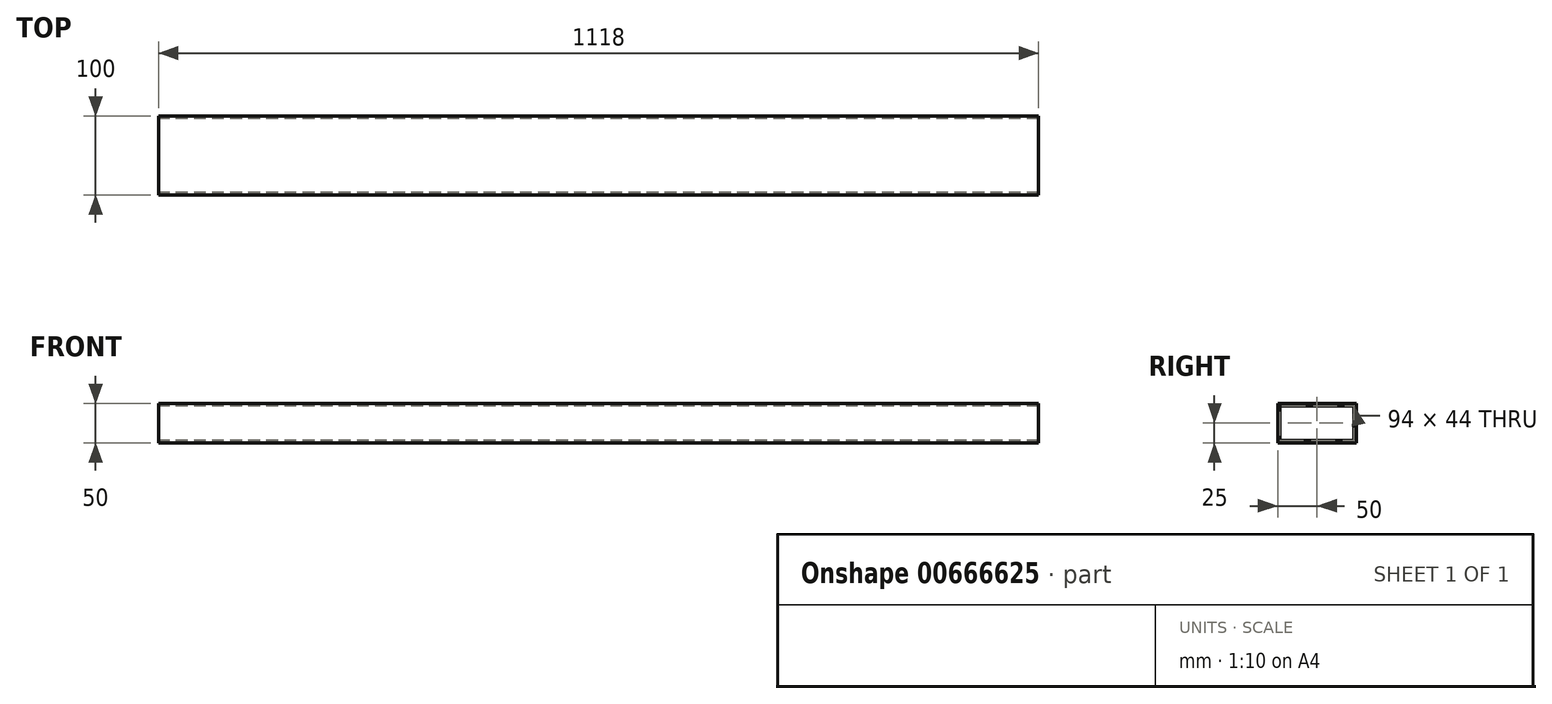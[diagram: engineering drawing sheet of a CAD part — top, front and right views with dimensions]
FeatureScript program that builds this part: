
annotation { "Feature Type Name" : "Feature", "Feature Type Description" : "" }
export const myFeature = defineFeature(function(context is Context, id is Id, definition is map)
    precondition{}
    {
        {
            var Q0;
            Q0=qCreatedBy(makeId("Right.planeOp"),FACE);
            var sketch = newSketch(context, id + "F0", { "sketchPlane" : qUnion([Q0])});
            skLineSegment(sketch, "E0.bottom", {"start": v(50, -25) * mm, "end": v(-50, -25) * mm});
            skLineSegment(sketch, "E0.top", {"start": v(50, 25) * mm, "end": v(-50, 25) * mm});
            skLineSegment(sketch, "E0.left", {"start": v(50, -25) * mm, "end": v(50, 25) * mm});
            skLineSegment(sketch, "E0.right", {"start": v(-50, -25) * mm, "end": v(-50, 25) * mm});
            skPoint(sketch, "E0.middle", {"position": v(0, 0) * mm});
            skLineSegment(sketch, "E1.bottom", {"start": v(47, -22) * mm, "end": v(-47, -22) * mm});
            skLineSegment(sketch, "E1.top", {"start": v(47, 22) * mm, "end": v(-47, 22) * mm});
            skLineSegment(sketch, "E1.left", {"start": v(47, -22) * mm, "end": v(47, 22) * mm});
            skLineSegment(sketch, "E1.right", {"start": v(-47, -22) * mm, "end": v(-47, 22) * mm});
            skSolve(sketch);
        }
        {
            var Q0;
            Q0=makeQuery(id+"F0.imprint","IMPRINT",FACE,{"disambiguationData":[TD([[makeQuery(id+"F0.imprint","IMPRINT",EDGE,{"derivedFrom":sQuery(id+"F0.wireOp",EDGE,"E0.bottom")}),-1.0]])]});
            extrude(context, id + "F1", {"entities" : qUnion([Q0]), "depth" : 1118 * mm, "offsetDistance" : 25 * mm});
        }
    });
